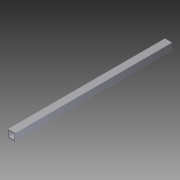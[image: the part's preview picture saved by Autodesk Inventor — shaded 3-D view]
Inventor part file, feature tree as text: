
AUTODESK INVENTOR PART (.ipt)
format: ipt  version: 2012 (Build 160160000, 160)  size: 74,240 bytes
history: native  units: in
note: dims shown in document units (in); Inventor stores cm internally (conversion verified against a paired STEP export)
features: extrude x1, sketch x1
ambient origin geometry x8: Origin, YZ Plane, XZ Plane, XY Plane, X Axis, Y Axis, Z Axis, Center Point
bodies: Solid1 (feature_tree)
feature tree (2):
  extrude  "Extrusion1"  Depth=1.0in
  sketch  "Sketch1"  dims[d0=1.0in d1=1.0in d2=0.125in d3=0.125in d4=0.125in d5=0.125in d6=21.75in d7=0.0in]
